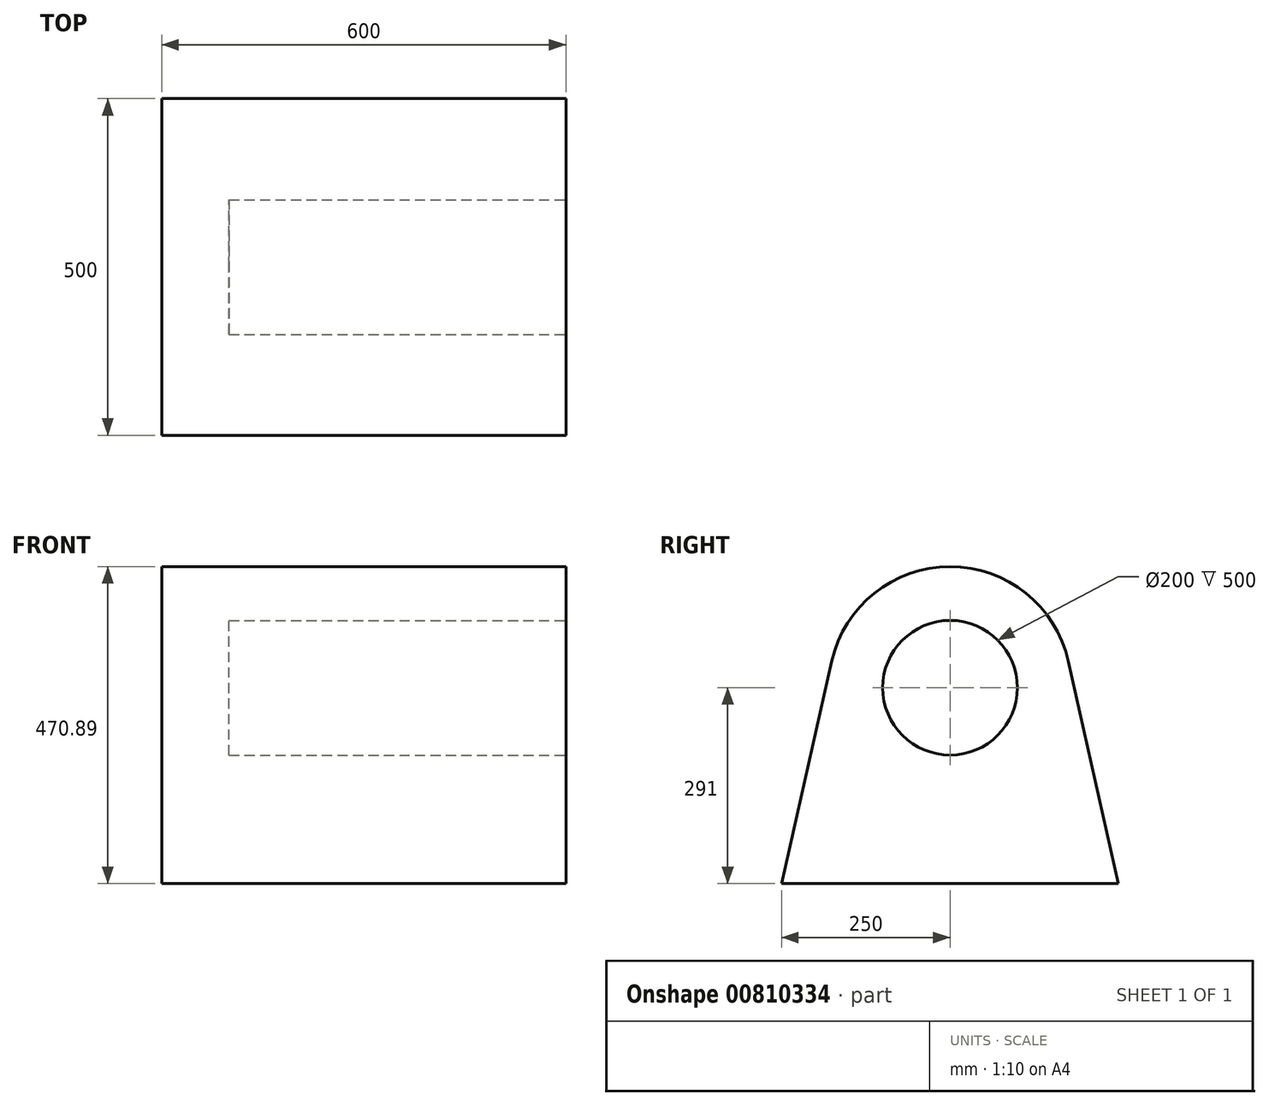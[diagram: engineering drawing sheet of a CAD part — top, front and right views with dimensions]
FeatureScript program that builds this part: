
annotation { "Feature Type Name" : "Feature", "Feature Type Description" : "" }
export const myFeature = defineFeature(function(context is Context, id is Id, definition is map)
    precondition{}
    {
        {
            var Q0;
            Q0=qCreatedBy(makeId("Right.planeOp"),FACE);
            var sketch = newSketch(context, id + "F0", { "sketchPlane" : qUnion([Q0])});
            skArc(sketch, "E0", {"start": v(175.48, 330.56) * mm, "mid": v(0, 470.89) * mm, "end": v(-175.48, 330.56) * mm});
            skLineSegment(sketch, "E1", {"start": v(-175.48, 330.56) * mm, "end": v(-250, 0) * mm});
            skLineSegment(sketch, "E2", {"start": v(175.48, 330.56) * mm, "end": v(250, 0) * mm});
            skLineSegment(sketch, "E3", {"start": v(250, 0) * mm, "end": v(-250, 0) * mm});
            skLineSegment(sketch, "E4", {"start": v(0, 607.76) * mm, "end": v(0, -25.76) * mm, "construction": true});
            skSolve(sketch);
        }
        {
            var Q0;
            Q0 = qSketchRegion(id + "F0", true);
            extrude(context, id + "F1", {"entities" : qUnion([Q0]), "depth" : 600 * mm, "offsetDistance" : 25.4 * mm});
        }
        {
            var Q0;
            Q0=makeQuery(id+"F1.opExtrude","CAP_FACE",FACE,{"disambiguationData":[OSD([sQuery(id+"F0.wireOp",EDGE,"E0"),sQuery(id+"F0.wireOp",EDGE,"E1"),sQuery(id+"F0.wireOp",EDGE,"E2"),sQuery(id+"F0.wireOp",EDGE,"E3")])],"isStart":false});
            var sketch = newSketch(context, id + "F2", { "sketchPlane" : qUnion([Q0])});
            skCircle(sketch, "E5", {"center": v(0, 291) * mm, "radius": 100 * mm});
            skPoint(sketch, "E5.centerSnap0", {"position": v(0, 470.89) * mm});
            skSolve(sketch);
        }
        {
            var Q0;
            Q0 = qSketchRegion(id + "F2", true);
            extrude(context, id + "F3", {"entities" : qUnion([Q0]), "operationType" : NewBodyOperationType.REMOVE, "oppositeDirection" : true, "depth" : 500 * mm, "offsetDistance" : 25.4 * mm});
        }
    });
